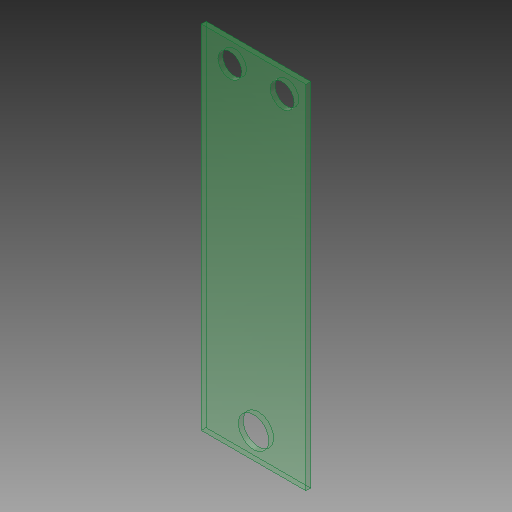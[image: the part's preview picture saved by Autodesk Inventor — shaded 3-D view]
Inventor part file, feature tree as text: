
AUTODESK INVENTOR PART (.ipt)
format: ipt  version: 2018.1 (Build 221171000, 171)  size: 116,736 bytes
history: native  units: mm
features: extrude x2, sketch x2, other x1
ambient origin geometry x8: Origin, YZ Plane, XZ Plane, XY Plane, X Axis, Y Axis, Z Axis, Center Point
bodies: Solid1 (feature_tree)
feature tree (5):
  parser-record x1  (decoder bookkeeping rows leaked as tree rows — omitted from the tree; the rows remain in map.json)
  extrude  "Extrusion1"  Depth=370.0mm
  extrude  "Extrusion2"  TaperAngle=0.0deg  [1 undecoded]
  sketch  "Sketch1"  dims[d0=110.0mm d1=370.0mm]
  sketch  "Sketch2"  dims[d2=5.0mm d3=0.0mm d4=32.0mm d7=26.0mm d10=5.0mm d11=0.0mm d13=25.0mm d14=25.0mm d15=55.0mm d16=50.0mm d17=22.5mm]
note: 1 required parameter value undecoded (feature->parameter linkage not recoverable at this tier; creation-order binding heuristic only, values carry confidence <= 0.55)
note: 1 file-system path scrubbed to <path> (originals preserved in map.json)
